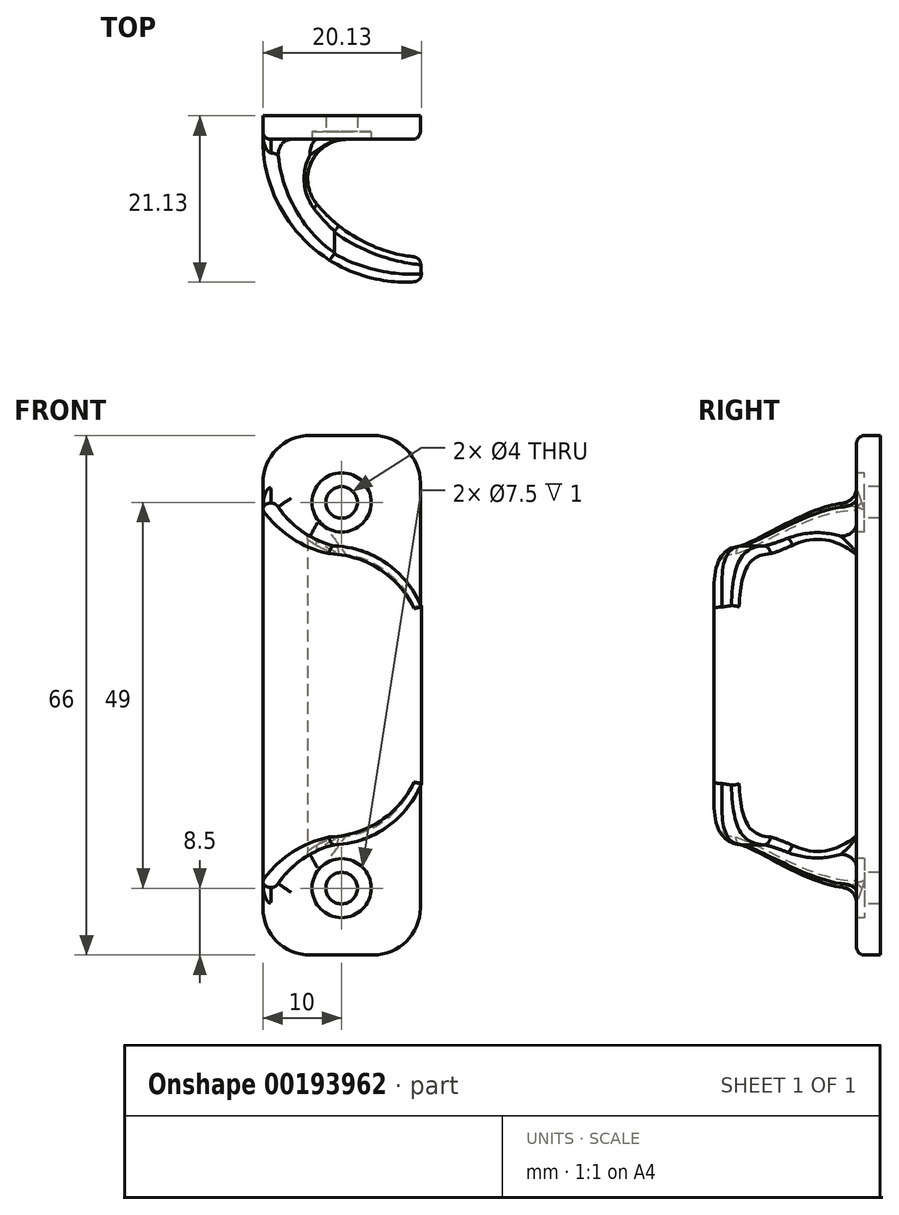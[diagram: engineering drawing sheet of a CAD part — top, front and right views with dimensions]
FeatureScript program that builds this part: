
annotation { "Feature Type Name" : "Feature", "Feature Type Description" : "" }
export const myFeature = defineFeature(function(context is Context, id is Id, definition is map)
    precondition{}
    {
        {
            var Q0;
            Q0=qCreatedBy(makeId("Top.planeOp"),FACE);
            var sketch = newSketch(context, id + "F0", { "sketchPlane" : qUnion([Q0])});
            skLineSegment(sketch, "E0", {"start": v(0, 0) * mm, "end": v(20, 0) * mm});
            skLineSegment(sketch, "E1", {"start": v(20, 0) * mm, "end": v(20, -3) * mm});
            skLineSegment(sketch, "E2", {"start": v(20, -3) * mm, "end": v(3, -3) * mm});
            skLineSegment(sketch, "E3", {"start": v(0, 0) * mm, "end": v(0, -3) * mm});
            skArc(sketch, "E4", {"start": v(3, -3) * mm, "mid": v(8.95, -13.4) * mm, "end": v(20, -18) * mm});
            skLineSegment(sketch, "E5", {"start": v(20, -18) * mm, "end": v(20.2, -21.02) * mm});
            skArc(sketch, "E6", {"start": v(0, -3) * mm, "mid": v(6.06, -16.53) * mm, "end": v(20.2, -21.02) * mm});
            skSolve(sketch);
        }
        {
            var Q0;
            Q0=makeQuery(id+"F0.imprint","IMPRINT",FACE,{"disambiguationData":[TD([[makeQuery(id+"F0.imprint","IMPRINT",EDGE,{"derivedFrom":sQuery(id+"F0.wireOp",EDGE,"E0")}),-1.0]])]});
            extrude(context, id + "F1", {"entities" : qUnion([Q0]), "depth" : 33 * mm});
        }
        {
            var Q0;
            Q0=qCreatedBy(makeId("Front.planeOp"),FACE);
            cPlane(context, id + "F2", {"entities" : qUnion([Q0]), "cplaneType" : CPlaneType.OFFSET, "offset" : 25 * mm, "width" : 150 * mm, "height" : 150 * mm});
        }
        {
            var Q0;
            Q0=qCreatedBy(id+"F2.planeOp",FACE);
            var sketch = newSketch(context, id + "F3", { "sketchPlane" : qUnion([Q0])});
            skArc(sketch, "E7", {"start": v(20.98, 7.8) * mm, "mid": v(17.13, 15.6) * mm, "end": v(9.1, 18.98) * mm});
            skArc(sketch, "E8", {"start": v(0, 32.2) * mm, "mid": v(2, 23.84) * mm, "end": v(9.1, 18.98) * mm});
            skLineSegment(sketch, "E9", {"start": v(0, 32.2) * mm, "end": v(-9.6, 32.2) * mm});
            skLineSegment(sketch, "E10", {"start": v(-9.6, 32.2) * mm, "end": v(-9.6, 39.98) * mm});
            skLineSegment(sketch, "E11", {"start": v(-9.6, 39.98) * mm, "end": v(28.6, 39.98) * mm});
            skLineSegment(sketch, "E12", {"start": v(28.6, 39.98) * mm, "end": v(28.6, 7.8) * mm});
            skLineSegment(sketch, "E13", {"start": v(28.6, 7.8) * mm, "end": v(20.98, 7.8) * mm});
            skSolve(sketch);
        }
        {
            var Q0;
            Q0=makeQuery(id+"F3.imprint","IMPRINT",FACE,{"disambiguationData":[TD([[makeQuery(id+"F3.imprint","IMPRINT",EDGE,{"derivedFrom":sQuery(id+"F3.wireOp",EDGE,"E7")}),-1.0]])]});
            extrude(context, id + "F4", {"entities" : qUnion([Q0]), "operationType" : NewBodyOperationType.REMOVE, "oppositeDirection" : true, "depth" : 22 * mm});
        }
        {
            var Q0;
            Q0=makeQuery(id+"F1.opExtrude","SWEPT_EDGE",EDGE,{"disambiguationData":[OSD([sQuery(id+"F0.wireOp",EDGE,"E2"),sQuery(id+"F0.wireOp",EDGE,"E4")])]});
            fillet(context, id + "F5", {"entities" : qUnion([Q0]), "radius" : 5 * mm, "tangentPropagation" : true, "allowEdgeOverflow" : false});
        }
        {
            var Q0;
            Q0=makeQuery(id+"F1.opExtrude","SWEPT_EDGE",EDGE,{"disambiguationData":[OSD([sQuery(id+"F0.wireOp",EDGE,"E5"),sQuery(id+"F0.wireOp",EDGE,"E6")])]});
            var Q1;
            Q1=makeQuery(id+"F1.opExtrude","SWEPT_EDGE",EDGE,{"disambiguationData":[OSD([sQuery(id+"F0.wireOp",EDGE,"E4"),sQuery(id+"F0.wireOp",EDGE,"E5")])]});
            var Q2;
            Q2=makeQuery(id+"F1.opExtrude","SWEPT_EDGE",EDGE,{"disambiguationData":[OSD([sQuery(id+"F0.wireOp",EDGE,"E1"),sQuery(id+"F0.wireOp",EDGE,"E2")])]});
            var Q3;
            Q3=makeQuery(id+"F4.boolean.opBoolean","INTERSECT",EDGE,{"derivedFrom":[makeQuery(id+"F1.opExtrude","CAP_FACE",FACE,{"disambiguationData":[OSD([sQuery(id+"F0.wireOp",EDGE,"E0"),sQuery(id+"F0.wireOp",EDGE,"E1"),sQuery(id+"F0.wireOp",EDGE,"E2"),sQuery(id+"F0.wireOp",EDGE,"E3"),sQuery(id+"F0.wireOp",EDGE,"E4"),sQuery(id+"F0.wireOp",EDGE,"E5"),sQuery(id+"F0.wireOp",EDGE,"E6")])],"isStart":false}),makeQuery(id+"F4.opExtrude","CAP_FACE",FACE,{"disambiguationData":[OSD([sQuery(id+"F3.wireOp",EDGE,"E7"),sQuery(id+"F3.wireOp",EDGE,"E8"),sQuery(id+"F3.wireOp",EDGE,"E9"),sQuery(id+"F3.wireOp",EDGE,"E10"),sQuery(id+"F3.wireOp",EDGE,"E11"),sQuery(id+"F3.wireOp",EDGE,"E12"),sQuery(id+"F3.wireOp",EDGE,"E13")])],"isStart":false})]});
            var Q4;
            {var subQ0=sQuery(id+"F0.wireOp",EDGE,"E3");var subQ1=sQuery(id+"F0.wireOp",EDGE,"E2");var subQ2=sQuery(id+"F0.wireOp",EDGE,"E6");Q4=makeQuery(id+"F4.boolean.opBoolean","SPLIT",EDGE,{"disambiguationData":[TD([makeQuery(id+"F1.opExtrude","CAP_FACE",FACE,{"disambiguationData":[OSD([sQuery(id+"F0.wireOp",EDGE,"E0"),sQuery(id+"F0.wireOp",EDGE,"E1"),subQ1,subQ0,sQuery(id+"F0.wireOp",EDGE,"E4"),sQuery(id+"F0.wireOp",EDGE,"E5"),subQ2])],"isStart":false})])],"derivedFrom":makeQuery(id+"F1.opExtrude","SWEPT_EDGE",EDGE,{"disambiguationData":[OSD([subQ0,subQ2])]})});}
            var Q5;
            Q5=makeQuery(id+"F4.boolean.opBoolean","INTERSECT",EDGE,{"derivedFrom":[makeQuery(id+"F1.opExtrude","SWEPT_FACE",FACE,{"disambiguationData":[OSD([sQuery(id+"F0.wireOp",EDGE,"E6")])]}),makeQuery(id+"F4.opExtrude","SWEPT_FACE",FACE,{"disambiguationData":[OSD([sQuery(id+"F3.wireOp",EDGE,"E8")])]})]});
            var Q6;
            Q6=makeQuery(id+"F4.boolean.opBoolean","INTERSECT",EDGE,{"derivedFrom":[makeQuery(id+"F1.opExtrude","SWEPT_FACE",FACE,{"disambiguationData":[OSD([sQuery(id+"F0.wireOp",EDGE,"E6")])]}),makeQuery(id+"F4.opExtrude","SWEPT_FACE",FACE,{"disambiguationData":[OSD([sQuery(id+"F3.wireOp",EDGE,"E7")])]})]});
            var Q7;
            Q7=makeQuery(id+"F4.boolean.opBoolean","INTERSECT",EDGE,{"derivedFrom":[makeQuery(id+"F1.opExtrude","SWEPT_FACE",FACE,{"disambiguationData":[OSD([sQuery(id+"F0.wireOp",EDGE,"E4")])]}),makeQuery(id+"F4.opExtrude","SWEPT_FACE",FACE,{"disambiguationData":[OSD([sQuery(id+"F3.wireOp",EDGE,"E8")])]})]});
            var Q8;
            Q8=makeQuery(id+"F4.boolean.opBoolean","INTERSECT",EDGE,{"derivedFrom":[makeQuery(id+"F1.opExtrude","SWEPT_FACE",FACE,{"disambiguationData":[OSD([sQuery(id+"F0.wireOp",EDGE,"E4")])]}),makeQuery(id+"F4.opExtrude","SWEPT_FACE",FACE,{"disambiguationData":[OSD([sQuery(id+"F3.wireOp",EDGE,"E7")])]})]});
            fillet(context, id + "F6", {"entities" : qUnion([Q0, Q1, Q2, Q3, Q4, Q5, Q6, Q7, Q8]), "radius" : 1 * mm, "tangentPropagation" : true, "allowEdgeOverflow" : false});
        }
        {
            var Q0;
            Q0=makeQuery(id+"F4.boolean.opBoolean","COPY",EDGE,{"derivedFrom":makeQuery(id+"F4.opExtrude","CAP_EDGE",EDGE,{"disambiguationData":[OSD([sQuery(id+"F3.wireOp",EDGE,"E8")])],"isStart":false})});
            fillet(context, id + "F7", {"entities" : qUnion([Q0]), "radius" : 2 * mm, "tangentPropagation" : true, "allowEdgeOverflow" : false});
        }
        {
            var Q0;
            Q0=makeQuery(id+"F1.opExtrude","CAP_EDGE",EDGE,{"disambiguationData":[OSD([sQuery(id+"F0.wireOp",EDGE,"E3")])],"isStart":false});
            var Q1;
            Q1=makeQuery(id+"F1.opExtrude","CAP_EDGE",EDGE,{"disambiguationData":[OSD([sQuery(id+"F0.wireOp",EDGE,"E1")])],"isStart":false});
            fillet(context, id + "F8", {"entities" : qUnion([Q0, Q1]), "radius" : 6 * mm, "tangentPropagation" : true, "allowEdgeOverflow" : false});
        }
        {
            var Q0;
            Q0=makeQuery(id+"F4.boolean.opBoolean","MERGE",FACE,{"derivedFrom":[makeQuery(id+"F1.opExtrude","SWEPT_FACE",FACE,{"disambiguationData":[OSD([sQuery(id+"F0.wireOp",EDGE,"E2")])]}),makeQuery(id+"F4.opExtrude","CAP_FACE",FACE,{"disambiguationData":[OSD([sQuery(id+"F3.wireOp",EDGE,"E7"),sQuery(id+"F3.wireOp",EDGE,"E8"),sQuery(id+"F3.wireOp",EDGE,"E9"),sQuery(id+"F3.wireOp",EDGE,"E10"),sQuery(id+"F3.wireOp",EDGE,"E11"),sQuery(id+"F3.wireOp",EDGE,"E12"),sQuery(id+"F3.wireOp",EDGE,"E13")])],"isStart":false})]});
            var sketch = newSketch(context, id + "F9", { "sketchPlane" : qUnion([Q0])});
            skPoint(sketch, "E14", {"position": v(10, 24.5) * mm});
            skPoint(sketch, "E14.positionSnap0", {"position": v(10, 32) * mm});
            skSolve(sketch);
        }
        {
            var Q0;
            Q0=sQuery(id+"F9.wireOp",VERTEX,"E14");
            var Q1;
            Q1=makeQuery(id+"F1.opExtrude","SWEPT_BODY",BODY,{"disambiguationData":[OSD([sQuery(id+"F0.wireOp",EDGE,"E0"),sQuery(id+"F0.wireOp",EDGE,"E1"),sQuery(id+"F0.wireOp",EDGE,"E2"),sQuery(id+"F0.wireOp",EDGE,"E3"),sQuery(id+"F0.wireOp",EDGE,"E4"),sQuery(id+"F0.wireOp",EDGE,"E5"),sQuery(id+"F0.wireOp",EDGE,"E6")])]});
            hole(context, id + "F10", {"style" : HoleStyle.C_BORE, "endStyle" : HoleEndStyle.THROUGH, "holeDiameter" : 4 * mm, "cBoreDiameter" : 7.5 * mm, "cBoreDepth" : 1 * mm, "locations" : qUnion([Q0]), "scope" : qUnion([Q1]), "isTappedThrough" : true});
        }
        {
            var Q0;
            Q0=makeQuery(id+"F1.opExtrude","SWEPT_BODY",BODY,{"disambiguationData":[OSD([sQuery(id+"F0.wireOp",EDGE,"E0"),sQuery(id+"F0.wireOp",EDGE,"E1"),sQuery(id+"F0.wireOp",EDGE,"E2"),sQuery(id+"F0.wireOp",EDGE,"E3"),sQuery(id+"F0.wireOp",EDGE,"E4"),sQuery(id+"F0.wireOp",EDGE,"E5"),sQuery(id+"F0.wireOp",EDGE,"E6")])]});
            var Q1;
            Q1=makeQuery(id+"F1.opExtrude","CAP_FACE",FACE,{"disambiguationData":[OSD([sQuery(id+"F0.wireOp",EDGE,"E0"),sQuery(id+"F0.wireOp",EDGE,"E1"),sQuery(id+"F0.wireOp",EDGE,"E2"),sQuery(id+"F0.wireOp",EDGE,"E3"),sQuery(id+"F0.wireOp",EDGE,"E4"),sQuery(id+"F0.wireOp",EDGE,"E5"),sQuery(id+"F0.wireOp",EDGE,"E6")])],"isStart":true});
            mirror(context, id + "F11", {"operationType" : NewBodyOperationType.ADD, "entities" : qUnion([Q0]), "mirrorPlane" : qUnion([Q1])});
        }
    });
